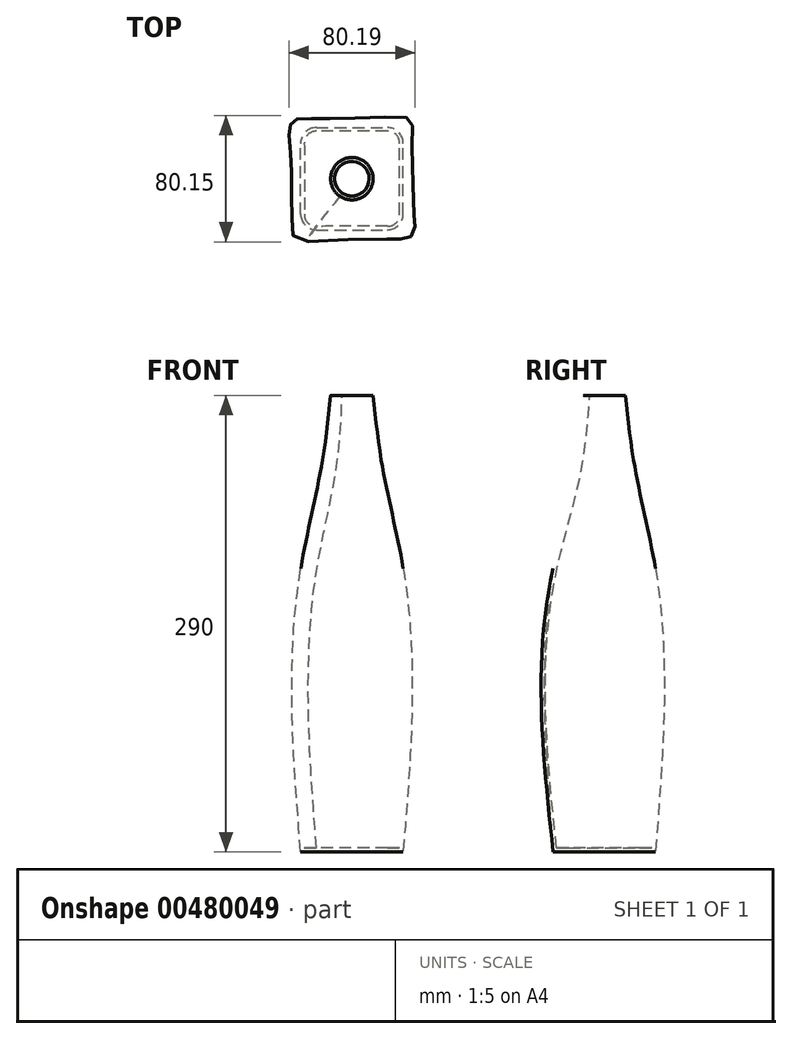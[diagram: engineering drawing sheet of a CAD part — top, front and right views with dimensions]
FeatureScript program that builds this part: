
annotation { "Feature Type Name" : "Feature", "Feature Type Description" : "" }
export const myFeature = defineFeature(function(context is Context, id is Id, definition is map)
    precondition{}
    {
        {
            var Q0;
            Q0=qCreatedBy(makeId("Top.planeOp"),FACE);
            var sketch = newSketch(context, id + "F0", { "sketchPlane" : qUnion([Q0])});
            skLineSegment(sketch, "E0.bottom", {"start": v(-22.5, -32.5) * mm, "end": v(22.55, -32.5) * mm});
            skLineSegment(sketch, "E0.top", {"start": v(-22.5, 32.46) * mm, "end": v(22.55, 32.46) * mm});
            skLineSegment(sketch, "E0.left", {"start": v(-32.5, -22.5) * mm, "end": v(-32.5, 22.46) * mm});
            skLineSegment(sketch, "E0.right", {"start": v(32.55, -22.5) * mm, "end": v(32.55, 22.46) * mm});
            skPoint(sketch, "E1.visualSharp", {"position": v(-32.5, -32.5) * mm});
            skArc(sketch, "E1.filletArc", {"start": v(-32.5, -22.5) * mm, "mid": v(-29.57, -29.57) * mm, "end": v(-22.5, -32.5) * mm});
            skPoint(sketch, "E2.visualSharp", {"position": v(32.55, -32.5) * mm});
            skArc(sketch, "E2.filletArc", {"start": v(22.55, -32.5) * mm, "mid": v(29.62, -29.57) * mm, "end": v(32.55, -22.5) * mm});
            skPoint(sketch, "E3.visualSharp", {"position": v(32.55, 32.46) * mm});
            skArc(sketch, "E3.filletArc", {"start": v(32.55, 22.46) * mm, "mid": v(29.62, 29.53) * mm, "end": v(22.55, 32.46) * mm});
            skPoint(sketch, "E4.visualSharp", {"position": v(-32.5, 32.46) * mm});
            skArc(sketch, "E4.filletArc", {"start": v(-22.5, 32.46) * mm, "mid": v(-29.57, 29.53) * mm, "end": v(-32.5, 22.46) * mm});
            skSolve(sketch);
        }
        {
            var Q0;
            Q0=qCreatedBy(makeId("Top.planeOp"),FACE);
            cPlane(context, id + "F1", {"entities" : qUnion([Q0]), "cplaneType" : CPlaneType.OFFSET, "offset" : 180 * mm, "width" : 150 * mm, "height" : 150 * mm});
        }
        {
            var Q0;
            Q0=qCreatedBy(id+"F1.planeOp",FACE);
            var sketch = newSketch(context, id + "F2", { "sketchPlane" : qUnion([Q0])});
            skLineSegment(sketch, "E5.bottom", {"start": v(-22.46, 32.52) * mm, "end": v(22.6, 32.52) * mm});
            skLineSegment(sketch, "E5.top", {"start": v(-22.46, -32.53) * mm, "end": v(22.6, -32.53) * mm});
            skLineSegment(sketch, "E5.left", {"start": v(-32.46, 22.52) * mm, "end": v(-32.46, -22.53) * mm});
            skLineSegment(sketch, "E5.right", {"start": v(32.6, 22.52) * mm, "end": v(32.6, -22.53) * mm});
            skPoint(sketch, "E6.visualSharp", {"position": v(-32.46, -32.53) * mm});
            skArc(sketch, "E6.filletArc", {"start": v(-32.46, -22.53) * mm, "mid": v(-29.53, -29.6) * mm, "end": v(-22.46, -32.53) * mm});
            skPoint(sketch, "E7.visualSharp", {"position": v(32.6, -32.53) * mm});
            skArc(sketch, "E7.filletArc", {"start": v(22.6, -32.53) * mm, "mid": v(29.68, -29.6) * mm, "end": v(32.6, -22.53) * mm});
            skPoint(sketch, "E8.visualSharp", {"position": v(32.6, 32.52) * mm});
            skArc(sketch, "E8.filletArc", {"start": v(32.6, 22.52) * mm, "mid": v(29.68, 29.6) * mm, "end": v(22.6, 32.52) * mm});
            skPoint(sketch, "E9.visualSharp", {"position": v(-32.46, 32.52) * mm});
            skArc(sketch, "E9.filletArc", {"start": v(-22.46, 32.52) * mm, "mid": v(-29.53, 29.6) * mm, "end": v(-32.46, 22.52) * mm});
            skSolve(sketch);
        }
        {
            var Q0;
            Q0=qCreatedBy(id+"F1.planeOp",FACE);
            cPlane(context, id + "F3", {"entities" : qUnion([Q0]), "cplaneType" : CPlaneType.OFFSET, "offset" : 70 * mm, "width" : 150 * mm, "height" : 150 * mm});
        }
        {
            var Q0;
            Q0=qCreatedBy(id+"F3.planeOp",FACE);
            var sketch = newSketch(context, id + "F4", { "sketchPlane" : qUnion([Q0])});
            skCircle(sketch, "E10", {"center": v(0, 0) * mm, "radius": 18.48 * mm});
            skSolve(sketch);
        }
        {
            var Q0;
            Q0=qCreatedBy(id+"F3.planeOp",FACE);
            cPlane(context, id + "F5", {"entities" : qUnion([Q0]), "cplaneType" : CPlaneType.OFFSET, "offset" : 40 * mm, "width" : 150 * mm, "height" : 150 * mm});
        }
        {
            var Q0;
            Q0=qCreatedBy(id+"F5.planeOp",FACE);
            var sketch = newSketch(context, id + "F6", { "sketchPlane" : qUnion([Q0])});
            skCircle(sketch, "E11", {"center": v(0, 0) * mm, "radius": 13.48 * mm});
            skSolve(sketch);
        }
        {
            var Q0;
            Q0=makeQuery(id+"F0.imprint","IMPRINT",FACE,{"disambiguationData":[TD([[makeQuery(id+"F0.imprint","IMPRINT",EDGE,{"derivedFrom":sQuery(id+"F0.wireOp",EDGE,"E0.bottom")}),1.0]])]});
            var Q1;
            Q1=makeQuery(id+"F2.imprint","IMPRINT",FACE,{"disambiguationData":[TD([[makeQuery(id+"F2.imprint","IMPRINT",EDGE,{"derivedFrom":sQuery(id+"F2.wireOp",EDGE,"E5.bottom")}),-1.0]])]});
            var Q2;
            Q2=makeQuery(id+"F4.imprint","IMPRINT",FACE,{"disambiguationData":[TD([[makeQuery(id+"F4.imprint","IMPRINT",EDGE,{"derivedFrom":sQuery(id+"F4.wireOp",EDGE,"E10")}),1.0]])]});
            var Q3;
            Q3=makeQuery(id+"F6.imprint","IMPRINT",FACE,{"disambiguationData":[TD([[makeQuery(id+"F6.imprint","IMPRINT",EDGE,{"derivedFrom":sQuery(id+"F6.wireOp",EDGE,"E11")}),1.0]])]});
            loft(context, id + "F7", {"sheetProfilesArray" : [{ "sheetProfileEntities" : qUnion([Q0]) }, { "sheetProfileEntities" : qUnion([Q1]) }, { "sheetProfileEntities" : qUnion([Q2]) }, { "sheetProfileEntities" : qUnion([Q3]) }]});
        }
        {
            var Q0;
            Q0=makeQuery(id+"F7.opLoft","CAP_FACE",FACE,{"disambiguationData":[OSD([makeQuery(id+"F6.imprint","IMPRINT",FACE,{"disambiguationData":[TD([[makeQuery(id+"F6.imprint","IMPRINT",EDGE,{"derivedFrom":sQuery(id+"F6.wireOp",EDGE,"E11")}),1.0]])]})])],"isStart":true});
            shell(context, id + "F8", {"entities" : qUnion([Q0]), "thickness" : 2.5 * mm});
        }
    });
